# Revit family: 10267 Приствольная решётка (квадратная) Р-03 Хоббика
name_source: partatom
category: Антураж
revit_build: Autodesk Revit 2018 (Build: 20180423_1000(x64)
units: mm (PartAtom-declared; Revit-internal decimal feet)

## family parameters
Всегда вертикально = Да
Источник визуального образа = Геометрия семейства
На основе рабочей плоскости = Нет
Общий = Нет
При загрузке вырезать с полостями = Нет
Точка расчета площади = Нет

## types (2) — shared parameters
URL = https://hobbyka.ru
Артикул товара = Арт. 10267
Высота = 22 мм
Группа модели = Решётки для деревьев
Изготовитель = ООО «Хоббика»
Изображение типоразмера = Приствольная решётка (квадратная) Р-03 Арт 10267.jpg
Материал изделия = Чугун
Цвет решетки = Чугун

## per-type parameters (varying)
| type | Версия 1,0 м | Версия 1,2 м | Диаметр внутренний | Длина | Описание |
| Версия 1,0 м | Да | Нет | 500 мм | 1000 мм | Приствольная решётка (квадратная) Р-03. Версия 1,0 м |
| Версия 1,2 м | Нет | Да | 600 мм | 1200 мм | Приствольная решётка (квадратная) Р-03. Версия 1,2 м |
